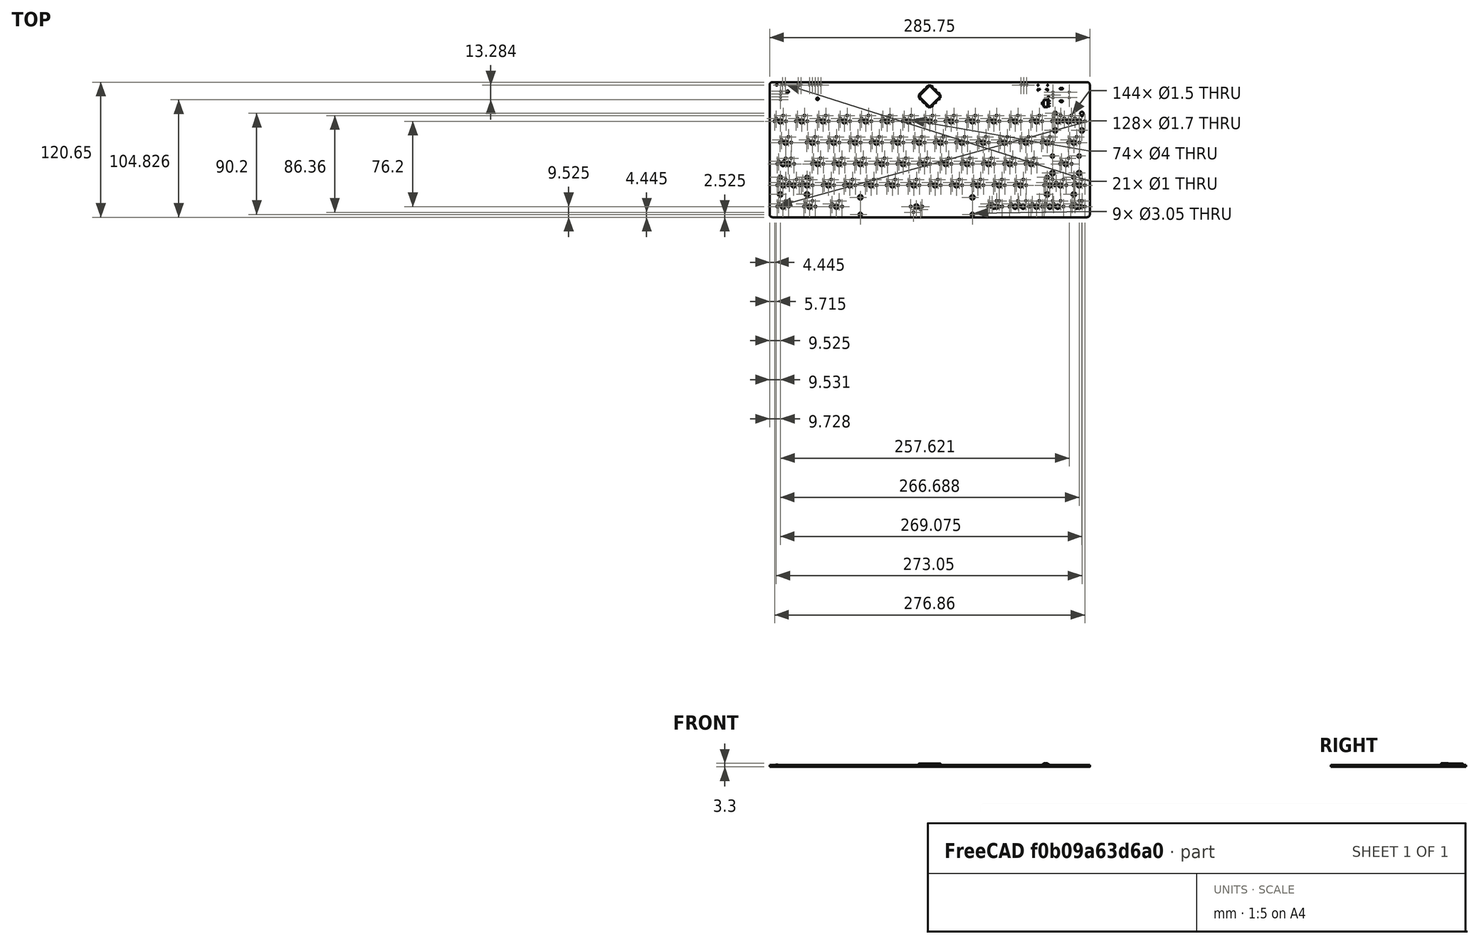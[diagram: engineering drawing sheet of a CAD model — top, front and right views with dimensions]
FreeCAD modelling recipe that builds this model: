
FCSTD DOCUMENT  (FreeCAD 0.19R23141 (Git))
Label: grabert_pcb
License: Creative Commons Attribution-NonCommercial
LicenseURL: http://creativecommons.org/licenses/by-nc/4.0/
objects: Part::Feature×5, App::Part×4, App::Link×4, PartDesign::CoordinateSystem×3, PartDesign::Point×2, Sketcher::SketchObject×1
note: 11 computed .brp shape members not serialized (recipe doc carries the construction recipe); baked Part::Feature solids carry a one-line shape summary decoded from their .brp

FEATURE [PartDesign::CoordinateSystem] Local_CS_4306
  AttacherType = Attacher::AttachEngine3D
FEATURE [Part::Feature] Pcb_4306
  shape: bbox 285.8 x 120.7 x 1.6 mm, 472 faces (baked)
FEATURE [Sketcher::SketchObject] PCB_Sketch_4306
  sketch-geometry (8):
    g0: LineSegment StartX=285.75 StartY=118.11 StartZ=0 EndX=285.75 EndY=2.54 EndZ=0
    g1: LineSegment StartX=283.21 StartY=120.65 StartZ=0 EndX=2.54 EndY=120.65 EndZ=0
    g2: LineSegment StartX=283.21 StartY=-3.29e-14 StartZ=0 EndX=2.54 EndY=-4e-16 EndZ=0
    g3: LineSegment StartX=-1.24e-14 StartY=118.11 StartZ=0 EndX=0 EndY=2.54 EndZ=0
    g4: ArcOfCircle CenterX=2.54 CenterY=118.11 CenterZ=0 NormalX=0 NormalY=0 NormalZ=1 AngleXU=0 Radius=2.54 StartAngle=1.5708 EndAngle=3.14159
    g5: ArcOfCircle CenterX=2.54 CenterY=2.54 CenterZ=0 NormalX=0 NormalY=0 NormalZ=1 AngleXU=0 Radius=2.54 StartAngle=3.14159 EndAngle=4.71239
    g6: ArcOfCircle CenterX=283.21 CenterY=118.11 CenterZ=0 NormalX=0 NormalY=0 NormalZ=1 AngleXU=0 Radius=2.54 StartAngle=0 EndAngle=1.5708
    g7: ArcOfCircle CenterX=283.21 CenterY=2.54 CenterZ=0 NormalX=0 NormalY=0 NormalZ=1 AngleXU=0 Radius=2.54 StartAngle=4.71239 EndAngle=6.28319
  constraints (8):
    c: Coincident(g3,g5)
    c: Coincident(g3,g4)
    c: Coincident(g2,g5)
    c: Coincident(g1,g4)
    c: Coincident(g2,g7)
    c: Coincident(g1,g6)
    c: Coincident(g0,g7)
    c: Coincident(g0,g6)
FEATURE [App::Part] Board_Geoms_4306
  Group = -> [Local_CS_4306,Pcb_4306,PCB_Sketch_4306]
  Origin = -> Origin
FEATURE [Part::Feature] Shape003  label=""C1"_C_0603_1608Metric_5db69710-2d0d-45d7-a742-beb49e07931f"
  Placement = pos=(248.92,107.315,0) rot=(0,0,1;1.5708rad)
  shape: bbox 0.8 x 1.6 x 0.8 mm, 28 faces (baked)
FEATURE [Part::Feature] Shape004  label=""U2"_LQFP_100_14x14mm_P05mm_719b990f-ae4c-490b-9cd7-5392cd54d5f2"
  Placement = pos=(142.875,107.95,0) rot=(0,0,1;0.785398rad)
  shape: bbox 19.95 x 19.95 x 1.5 mm, 1544 faces (baked)
FEATURE [Part::Feature] Shape005  label=""R2"_R_0603_1608Metric_b3f198d9-8440-4a91-92b4-b595c153e976"
  Placement = pos=(6.35,118.11,0) rot=(0,0,1;0rad)
  shape: bbox 1.6 x 0.8 x 0.45 mm, 26 faces (baked)
FEATURE [App::Link] _C1__C_0603_1608Metric_5db69710_2d0d_45d7_a742_beb49e07931f_ln_  label=""C2"_C_0603_1608Metric_bc751e6e-ea76-4202-bdc8-b0e3f3729951"
  LinkPlacement = pos=(240.538,107.315,0) rot=(0,0,1;1.5708rad)
  LinkedObject = -> Shape003
  Placement = pos=(240.538,107.315,0) rot=(0,0,1;1.5708rad)
FEATURE [Part::Feature] Shape006  label=""U1"_SOT_223_c46af92f-9185-4327-9a7a-dfaa81b7fe2d"
  Placement = pos=(246.38,101.6,0) rot=(0,0,1;3.14159rad)
  shape: bbox 7 x 6.5 x 1.7 mm, 78 faces (baked)
FEATURE [App::Link] _R2__R_0603_1608Metric_b3f198d9_8440_4a91_92b4_b595c153e976_ln_  label=""R3"_R_0603_1608Metric_eb4d33d1-0a7c-470d-97ed-5c512bd76df8"
  LinkPlacement = pos=(246.38,107.315,0) rot=(0,0,-1;1.5708rad)
  LinkedObject = -> Shape005
  Placement = pos=(246.38,107.315,0) rot=(0,0,-1;1.5708rad)
FEATURE [App::Link] _R2__R_0603_1608Metric_b3f198d9_8440_4a91_92b4_b595c153e976_ln_001  label=""R4"_R_0603_1608Metric_edde6bde-11c9-460a-868f-a0e0e945686d"
  LinkPlacement = pos=(244.475,107.315,0) rot=(0,0,-1;1.5708rad)
  LinkedObject = -> Shape005
  Placement = pos=(244.475,107.315,0) rot=(0,0,-1;1.5708rad)
FEATURE [App::Link] _R2__R_0603_1608Metric_b3f198d9_8440_4a91_92b4_b595c153e976_ln_002  label=""R1"_R_0603_1608Metric_f86d962d-e1b5-4395-8a34-b8604b4393b0"
  LinkPlacement = pos=(20.32,118.11,0) rot=(0,0,1;3.14159rad)
  LinkedObject = -> Shape005
  Placement = pos=(20.32,118.11,0) rot=(0,0,1;3.14159rad)
FEATURE [App::Part] Top_4306
  Group = -> [Shape003,Shape004,Shape005,_C1__C_0603_1608Metric_5db69710_2d0d_45d7_a742_beb49e07931f_ln_,Shape006,_R2__R_0603_1608Metric_b3f198d9_8440_4a91_92b4_b595c153e976_ln_,_R2__R_0603_1608Metric_b3f198d9_8440_4a91_92b4_b595c153e976_ln_001,_R2__R_0603_1608Metric_b3f198d9_8440_4a91_92b4_b595c153e976_ln_002]
  Origin = -> Origin003
FEATURE [App::Part] Step_Models_4306
  Group = -> [Top_4306]
  Origin = -> Origin002
FEATURE [PartDesign::Point] Point_1
  AttacherType = Attacher::AttachEnginePoint
  MapMode = 36
  Placement = pos=(9.525,85.725,0) rot=(1,0,0;1.5708rad)
  Support = -> [Pcb_4306]
FEATURE [PartDesign::Point] Point_2
  AttacherType = Attacher::AttachEnginePoint
  MapMode = 36
  Placement = pos=(9.7282,112.446,0) rot=(1,0,0;1.5708rad)
  Support = -> [Pcb_4306]
FEATURE [PartDesign::CoordinateSystem] LCS_2
  AttacherType = Attacher::AttachEngine3D
  MapMode = 1
  Placement = pos=(9.7282,112.446,0) rot=(0,0,1;0rad)
  Support = -> [Point_2]
FEATURE [PartDesign::CoordinateSystem] LCS_3
  AttacherType = Attacher::AttachEngine3D
  MapMode = 1
  Placement = pos=(9.525,85.725,0) rot=(0,0,1;0rad)
  Support = -> [Point_1]
FEATURE [App::Part] Board_4306  label="grabert_pcb"
  Group = -> [Board_Geoms_4306,Step_Models_4306,Point_1,Point_2,LCS_2,LCS_3]
  Origin = -> Origin001
